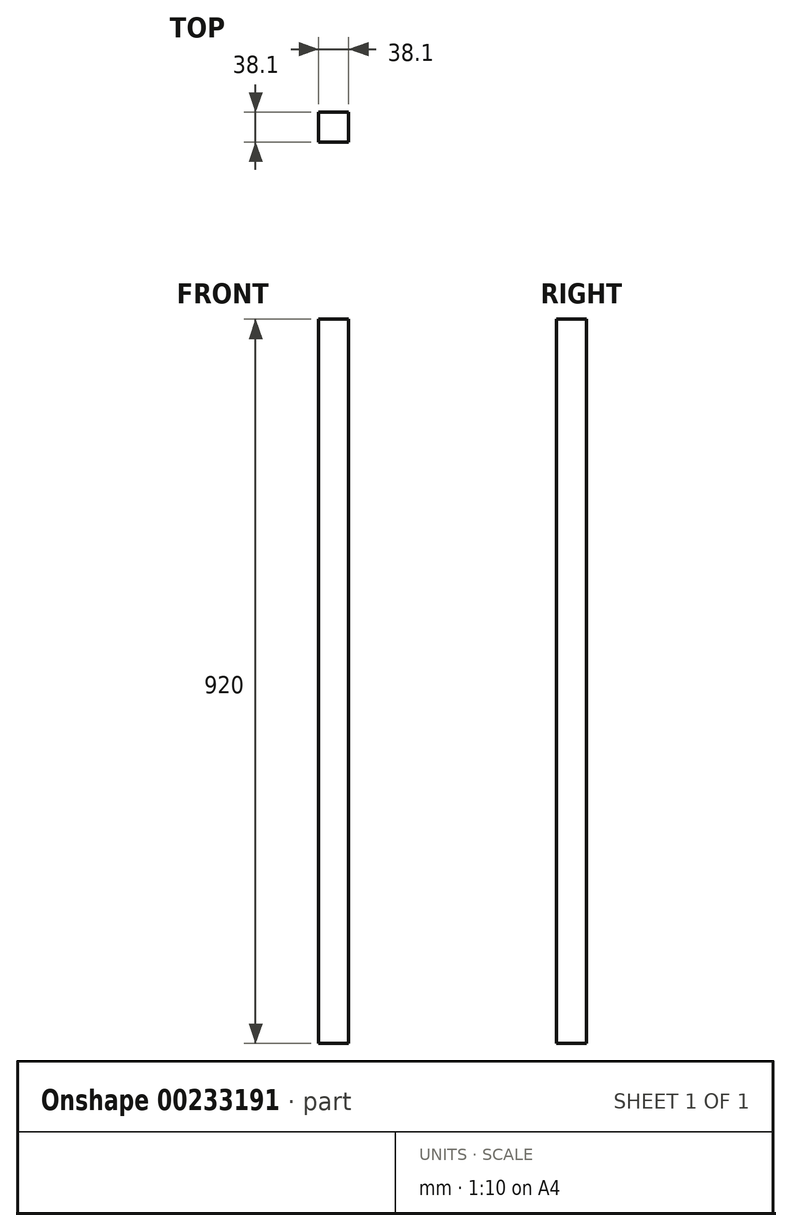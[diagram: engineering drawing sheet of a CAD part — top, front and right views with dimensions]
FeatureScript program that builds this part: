
annotation { "Feature Type Name" : "Feature", "Feature Type Description" : "" }
export const myFeature = defineFeature(function(context is Context, id is Id, definition is map)
    precondition{}
    {
        {
            var Q0;
            Q0=qCreatedBy(makeId("Front.planeOp"),FACE);
            var sketch = newSketch(context, id + "F0", { "sketchPlane" : qUnion([Q0])});
            skLineSegment(sketch, "E0.bottom", {"start": v(-17.2, 908.42) * mm, "end": v(20.9, 908.42) * mm});
            skLineSegment(sketch, "E0.top", {"start": v(-17.2, -11.58) * mm, "end": v(20.9, -11.58) * mm});
            skLineSegment(sketch, "E0.left", {"start": v(-17.2, 908.42) * mm, "end": v(-17.2, -11.58) * mm});
            skLineSegment(sketch, "E0.right", {"start": v(20.9, 908.42) * mm, "end": v(20.9, -11.58) * mm});
            skSolve(sketch);
        }
        {
            var Q0;
            Q0 = qSketchRegion(id + "F0", true);
            extrude(context, id + "F1", {"entities" : qUnion([Q0]), "depth" : 38.1 * mm});
        }
    });
